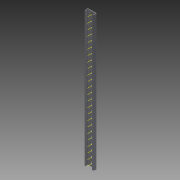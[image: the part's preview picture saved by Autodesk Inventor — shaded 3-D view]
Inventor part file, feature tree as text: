
AUTODESK INVENTOR PART (.ipt)
format: ipt  version: 2015 (Build 190159000, 159)  size: 439,296 bytes
history: native  units: in
note: dims shown in document units (in); Inventor stores cm internally (conversion verified against a paired STEP export)
features: other x27, boolean_combine x1, extrude x1, pattern_linear x1, plane x1, imported_body x1, sketch x1
ambient origin geometry x8: Origin, YZ Plane, XZ Plane, XY Plane, X Axis, Y Axis, Z Axis, Center Point
bodies: Body1 (feature_tree)
feature tree (33):
  boolean_combine  "Combine1"
  other  "Linear Slide"
  other  "Work Axis1"
  extrude  "Extrusion1"  TaperAngle=0.0deg  [1 undecoded]
  pattern_linear  "Rectangular Pattern1"  Spacing1=0.0in  [1 undecoded]
  plane  "Work Plane3"
  imported_body  "Base1"
  other  "Work Point1"
  other  "Work Axis2"
  sketch  "Sketch1"  dims[d0=9.4488in d2=0.5in d4=0.0in d5=0.0in d6=0.0in d9=-12.0in d10=0.0in]
  other  "Work Axis46"
  other  "Work Axis47"
  other  "Work Axis48"
  other  "Work Axis49"
  other  "Work Axis50"
  other  "Work Axis51"
  other  "Work Axis52"
  other  "Work Axis53"
  other  "Work Axis54"
  other  "Work Axis55"
  other  "Work Axis56"
  other  "Work Axis57"
  other  "Work Axis69"
  other  "Work Axis70"
  other  "Work Axis71"
  other  "Work Axis72"
  other  "Work Axis73"
  other  "Work Axis74"
  other  "Work Axis75"
  other  "Work Axis76"
  other  "bottom plane"
  other  "Work Axis101"
  other  "Work Axis102"
note: 2 required parameter values undecoded (feature->parameter linkage not recoverable at this tier; creation-order binding heuristic only, values carry confidence <= 0.55)
